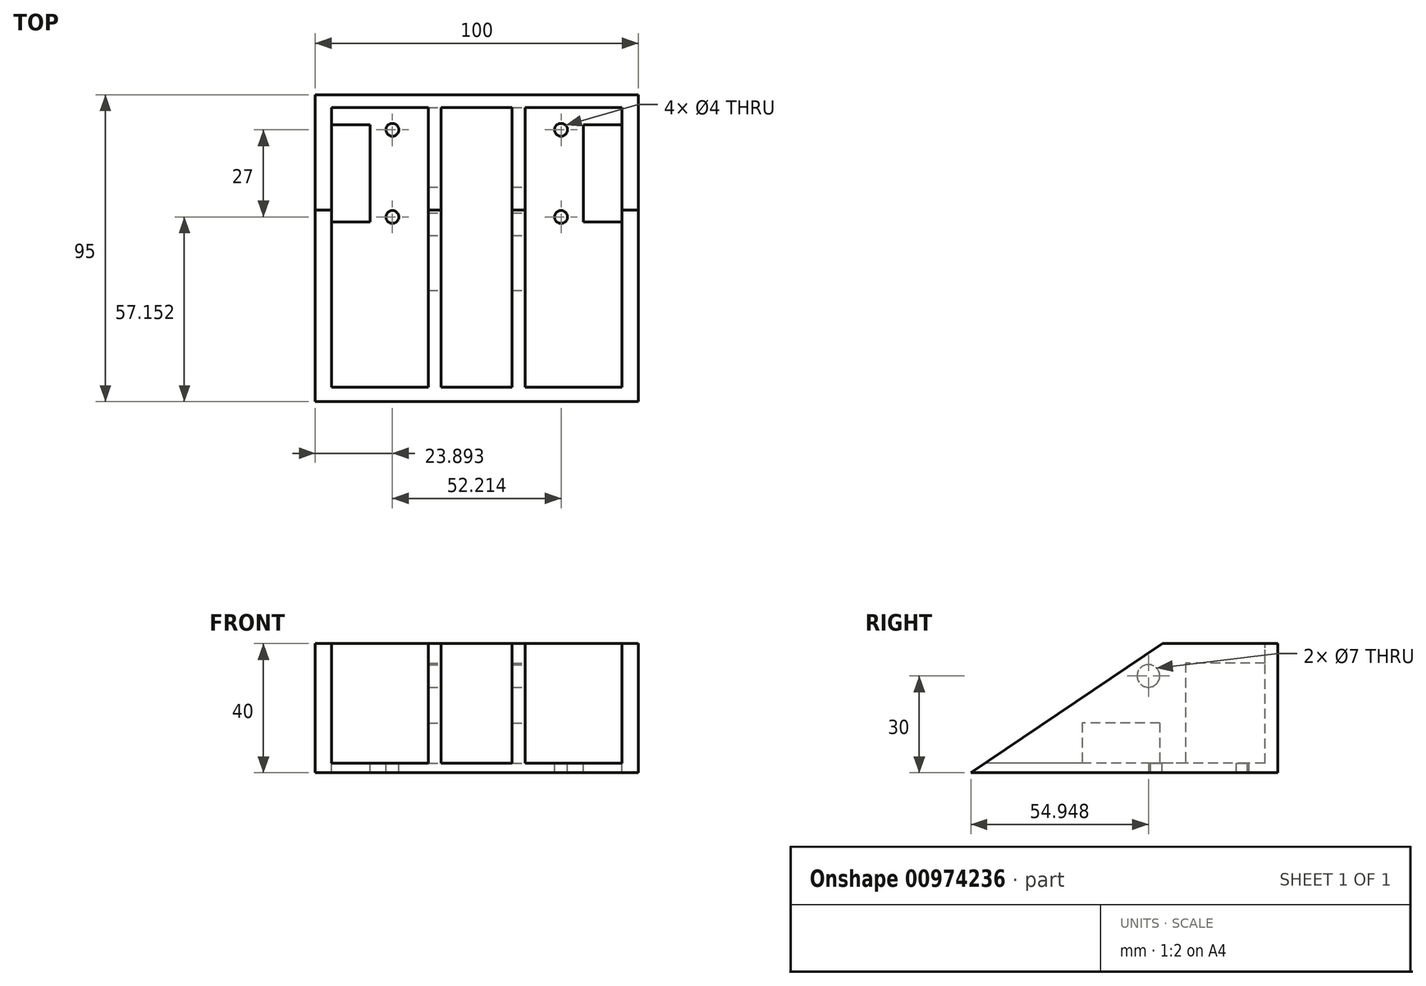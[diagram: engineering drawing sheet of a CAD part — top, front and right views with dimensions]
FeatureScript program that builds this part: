
annotation { "Feature Type Name" : "Feature", "Feature Type Description" : "" }
export const myFeature = defineFeature(function(context is Context, id is Id, definition is map)
    precondition{}
    {
        {
            var Q0;
            Q0=qCreatedBy(makeId("Right.planeOp"),FACE);
            var sketch = newSketch(context, id + "F0", { "sketchPlane" : qUnion([Q0])});
            skLineSegment(sketch, "E0", {"start": v(-35.7, 40) * mm, "end": v(0, 40) * mm});
            skLineSegment(sketch, "E1", {"start": v(0, 40) * mm, "end": v(0, 0) * mm});
            skLineSegment(sketch, "E2", {"start": v(0, 0) * mm, "end": v(-95, 0) * mm});
            skLineSegment(sketch, "E3", {"start": v(-95, 0) * mm, "end": v(-35.7, 40) * mm});
            skSolve(sketch);
        }
        {
            var Q0;
            Q0=makeQuery(id+"F0.imprint","IMPRINT",FACE,{"disambiguationData":[TD([[makeQuery(id+"F0.imprint","IMPRINT",EDGE,{"derivedFrom":sQuery(id+"F0.wireOp",EDGE,"E0")}),-1.0]])]});
            extrude(context, id + "F1", {"entities" : qUnion([Q0]), "endBound" : BoundingType.SYMMETRIC, "depth" : 100 * mm, "offsetDistance" : 25 * mm});
        }
        {
            var Q0;
            Q0=makeQuery(id+"F1.opExtrude","SWEPT_FACE",FACE,{"disambiguationData":[OSD([sQuery(id+"F0.wireOp",EDGE,"E0")])]});
            var sketch = newSketch(context, id + "F2", { "sketchPlane" : qUnion([Q0])});
            skLineSegment(sketch, "E4.bottom", {"start": v(-45, -4) * mm, "end": v(-15, -4) * mm});
            skLineSegment(sketch, "E4.top", {"start": v(-45, -95) * mm, "end": v(-15, -95) * mm});
            skLineSegment(sketch, "E4.left", {"start": v(-45, -4) * mm, "end": v(-45, -95) * mm});
            skLineSegment(sketch, "E4.right", {"start": v(-15, -4) * mm, "end": v(-15, -95) * mm});
            skLineSegment(sketch, "E5.bottom", {"start": v(15, -4) * mm, "end": v(45, -4) * mm});
            skLineSegment(sketch, "E5.top", {"start": v(15, -95) * mm, "end": v(45, -95) * mm});
            skLineSegment(sketch, "E5.left", {"start": v(15, -4) * mm, "end": v(15, -95) * mm});
            skLineSegment(sketch, "E5.right", {"start": v(45, -4) * mm, "end": v(45, -95) * mm});
            skLineSegment(sketch, "E6.bottom", {"start": v(-11, -4) * mm, "end": v(11, -4) * mm});
            skLineSegment(sketch, "E6.top", {"start": v(-11, -95) * mm, "end": v(11, -95) * mm});
            skLineSegment(sketch, "E6.left", {"start": v(-11, -4) * mm, "end": v(-11, -95) * mm});
            skLineSegment(sketch, "E6.right", {"start": v(11, -4) * mm, "end": v(11, -95) * mm});
            skSolve(sketch);
        }
        {
            var Q0;
            Q0 = qSketchRegion(id + "F2", true);
            extrude(context, id + "F3", {"entities" : qUnion([Q0]), "operationType" : NewBodyOperationType.REMOVE, "oppositeDirection" : true, "depth" : 37 * mm, "offsetDistance" : 25 * mm});
        }
        {
            var Q0;
            Q0=makeQuery(id+"F3.boolean.opBoolean","COPY",FACE,{"derivedFrom":makeQuery(id+"F3.opExtrude","SWEPT_FACE",FACE,{"disambiguationData":[OSD([sQuery(id+"F2.wireOp",EDGE,"E5.left")])]})});
            var sketch = newSketch(context, id + "F4", { "sketchPlane" : qUnion([Q0])});
            skLineSegment(sketch, "E7.bottom", {"start": v(-60.55, 3) * mm, "end": v(-36.55, 3) * mm});
            skLineSegment(sketch, "E7.top", {"start": v(-60.55, 15.45) * mm, "end": v(-36.55, 15.45) * mm});
            skLineSegment(sketch, "E7.left", {"start": v(-60.55, 3) * mm, "end": v(-60.55, 15.45) * mm});
            skLineSegment(sketch, "E7.right", {"start": v(-36.55, 3) * mm, "end": v(-36.55, 15.45) * mm});
            skCircle(sketch, "E8", {"center": v(-40.05, 30) * mm, "radius": 3.5 * mm});
            skLineSegment(sketch, "E9.bottom", {"start": v(-28.55, 3) * mm, "end": v(-4, 3) * mm});
            skLineSegment(sketch, "E9.top", {"start": v(-28.55, 34) * mm, "end": v(-4, 34) * mm});
            skLineSegment(sketch, "E9.left", {"start": v(-28.55, 3) * mm, "end": v(-28.55, 34) * mm});
            skLineSegment(sketch, "E9.right", {"start": v(-4, 3) * mm, "end": v(-4, 34) * mm});
            skSolve(sketch);
        }
        {
            var Q0;
            Q0 = qSketchRegion(id + "F4", true);
            var Q1;
            Q1=makeQuery(id+"F3.boolean.opBoolean","COPY",FACE,{"derivedFrom":makeQuery(id+"F3.opExtrude","SWEPT_FACE",FACE,{"disambiguationData":[OSD([sQuery(id+"F2.wireOp",EDGE,"E4.right")])]})});
            extrude(context, id + "F5", {"entities" : qUnion([Q0]), "operationType" : NewBodyOperationType.REMOVE, "endBound" : BoundingType.UP_TO_SURFACE, "oppositeDirection" : true, "depth" : 25 * mm, "endBoundEntityFace" : qUnion([Q1]), "offsetDistance" : 25 * mm});
        }
        {
            var Q0;
            Q0=makeQuery(id+"F5.boolean.opBoolean","MERGE",FACE,{"derivedFrom":[makeQuery(id+"F3.boolean.opBoolean","COPY",FACE,{"derivedFrom":makeQuery(id+"F3.opExtrude","CAP_FACE",FACE,{"disambiguationData":[OSD([sQuery(id+"F2.wireOp",EDGE,"E4.bottom"),sQuery(id+"F2.wireOp",EDGE,"E4.top"),sQuery(id+"F2.wireOp",EDGE,"E4.left"),sQuery(id+"F2.wireOp",EDGE,"E4.right")])],"isStart":false})}),makeQuery(id+"F3.boolean.opBoolean","COPY",FACE,{"derivedFrom":makeQuery(id+"F3.opExtrude","CAP_FACE",FACE,{"disambiguationData":[OSD([sQuery(id+"F2.wireOp",EDGE,"E5.bottom"),sQuery(id+"F2.wireOp",EDGE,"E5.top"),sQuery(id+"F2.wireOp",EDGE,"E5.left"),sQuery(id+"F2.wireOp",EDGE,"E5.right")])],"isStart":false})}),makeQuery(id+"F3.boolean.opBoolean","COPY",FACE,{"derivedFrom":makeQuery(id+"F3.opExtrude","CAP_FACE",FACE,{"disambiguationData":[OSD([sQuery(id+"F2.wireOp",EDGE,"E6.bottom"),sQuery(id+"F2.wireOp",EDGE,"E6.top"),sQuery(id+"F2.wireOp",EDGE,"E6.left"),sQuery(id+"F2.wireOp",EDGE,"E6.right")])],"isStart":false})})],"fromTools":[makeQuery(id+"F5.opExtrude","SWEPT_FACE",FACE,{"disambiguationData":[OSD([sQuery(id+"F4.wireOp",EDGE,"E7.bottom")])]}),makeQuery(id+"F5.opExtrude","SWEPT_FACE",FACE,{"disambiguationData":[OSD([sQuery(id+"F4.wireOp",EDGE,"E9.bottom")])]})]});
            var sketch = newSketch(context, id + "F6", { "sketchPlane" : qUnion([Q0])});
            skLineSegment(sketch, "E10.bottom", {"start": v(-45, -9.35) * mm, "end": v(-33, -9.35) * mm});
            skLineSegment(sketch, "E10.top", {"start": v(-45, -39.35) * mm, "end": v(-33, -39.35) * mm});
            skLineSegment(sketch, "E10.left", {"start": v(-45, -9.35) * mm, "end": v(-45, -39.35) * mm});
            skLineSegment(sketch, "E10.right", {"start": v(-33, -9.35) * mm, "end": v(-33, -39.35) * mm});
            skLineSegment(sketch, "E11.bottom", {"start": v(33, -9.35) * mm, "end": v(45, -9.35) * mm});
            skLineSegment(sketch, "E11.top", {"start": v(33, -39.35) * mm, "end": v(45, -39.35) * mm});
            skLineSegment(sketch, "E11.left", {"start": v(33, -9.35) * mm, "end": v(33, -39.35) * mm});
            skLineSegment(sketch, "E11.right", {"start": v(45, -9.35) * mm, "end": v(45, -39.35) * mm});
            skCircle(sketch, "E12", {"center": v(-26.1, -10.85) * mm, "radius": 2 * mm});
            skCircle(sketch, "E13", {"center": v(-26.1, -37.85) * mm, "radius": 2 * mm});
            skCircle(sketch, "E14", {"center": v(26.1, -10.85) * mm, "radius": 2 * mm});
            skCircle(sketch, "E15", {"center": v(26.1, -37.85) * mm, "radius": 2 * mm});
            skLineSegment(sketch, "E16", {"start": v(26.1, -24.35) * mm, "end": v(45, -24.35) * mm, "construction": true});
            skSolve(sketch);
        }
        {
            var Q0;
            Q0 = qSketchRegion(id + "F6", true);
            extrude(context, id + "F7", {"entities" : qUnion([Q0]), "operationType" : NewBodyOperationType.REMOVE, "endBound" : BoundingType.THROUGH_ALL, "oppositeDirection" : true, "depth" : 25 * mm, "offsetDistance" : 25 * mm});
        }
    });
